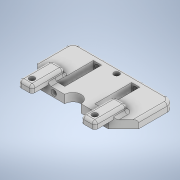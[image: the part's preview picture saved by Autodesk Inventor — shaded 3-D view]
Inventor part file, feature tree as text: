
AUTODESK INVENTOR PART (.ipt)
format: ipt  version: 2020 (Build 240168000, 168)  size: 274,432 bytes
history: native  units: in
note: dims shown in document units (in); Inventor stores cm internally (conversion verified against a paired STEP export)
features: extrude x5, sketch x5, fillet x3
ambient origin geometry x8: Origin, YZ Plane, XZ Plane, XY Plane, X Axis, Y Axis, Z Axis, Center Point
bodies: Solid1 (feature_tree)
feature tree (13):
  extrude  "Extrusion1"  Depth=0.2362in
  fillet  "Fillet1"  Radius=0.2362in
  extrude  "Extrusion2"  Depth=0.4724in
  extrude  "Extrusion6"  TaperAngle=135.0deg  [1 undecoded]
  extrude  "Extrusion8"  TaperAngle=135.0deg  [1 undecoded]
  extrude  "Extrusion9"  Depth=0.0787in
  fillet  "Fillet3"  Radius=0.1575in
  fillet  "Fillet4"  Radius=0.3937in
  sketch  "Sketch1"  dims[d0=2.9134in d1=2.9134in d2=0.2362in d3=0.0in]
  sketch  "Sketch2"  dims[d4=0.1969in d5=0.4724in]
  sketch  "Sketch6"  dims[d6=0.7874in d7=135.0deg]
  sketch  "Sketch8"  dims[d8=0.7874in d9=135.0deg]
  sketch  "Sketch9"  dims[d10=0.1575in d11=0.1575in d12=0.1575in d13=0.3937in d14=0.0in d29=0.1575in d30=0.2362in d31=1.063in d32=0.2362in d33=1.063in d34=0.3937in d35=0.0in d44=0.1575in d45=0.1575in d46=1.9685in d47=0.0in d48=0.1575in d49=0.1575in d50=0.3937in d51=0.9449in d52=0.3937in d53=0.9449in d54=0.1969in d55=0.0in d56=0.0787in d57=0.0787in]
note: 2 required parameter values undecoded (feature->parameter linkage not recoverable at this tier; creation-order binding heuristic only, values carry confidence <= 0.55)
